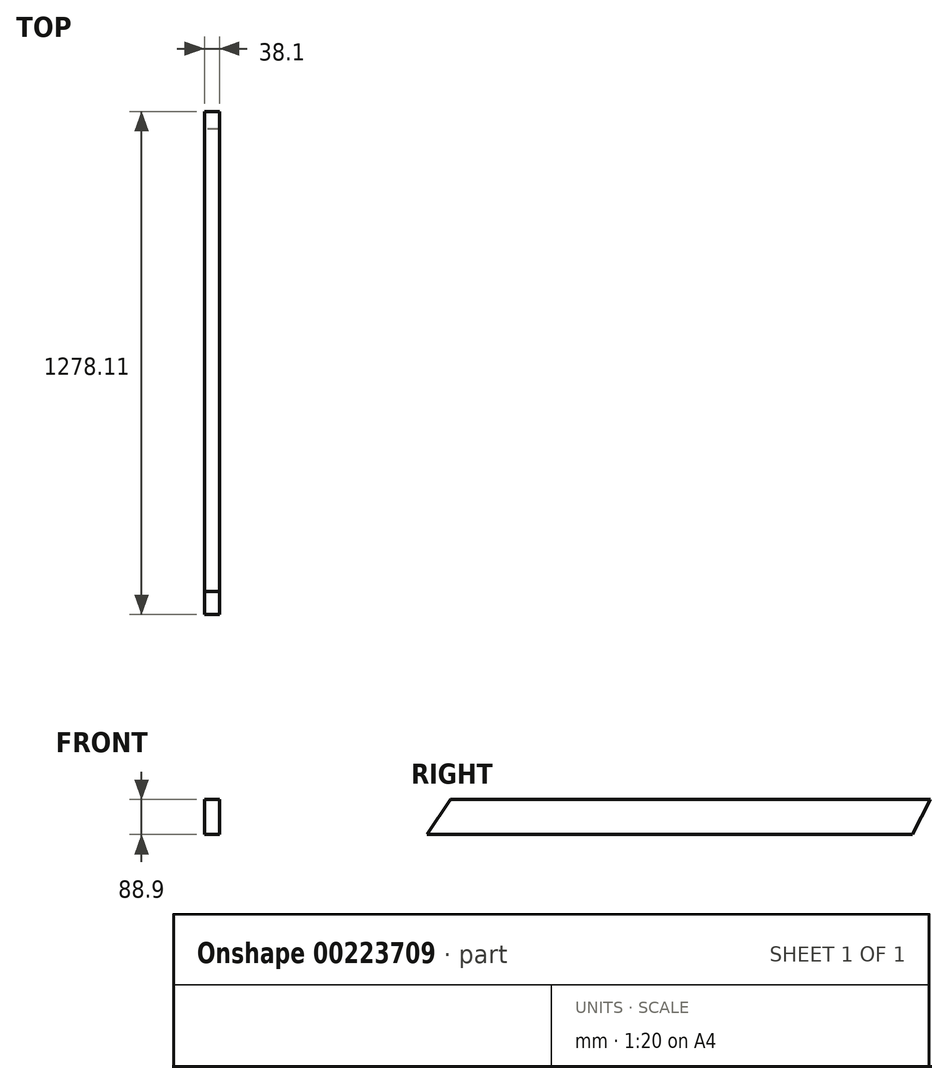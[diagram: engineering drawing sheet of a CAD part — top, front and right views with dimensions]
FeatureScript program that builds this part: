
annotation { "Feature Type Name" : "Feature", "Feature Type Description" : "" }
export const myFeature = defineFeature(function(context is Context, id is Id, definition is map)
    precondition{}
    {
        {
            var Q0;
            Q0=qCreatedBy(makeId("Right.planeOp"),FACE);
            var sketch = newSketch(context, id + "F0", { "sketchPlane" : qUnion([Q0])});
            skLineSegment(sketch, "E0.bottom", {"start": v(-609.42, -26.03) * mm, "end": v(609.78, -26.03) * mm});
            skLineSegment(sketch, "E0.top", {"start": v(-668.33, -114.93) * mm, "end": v(564.48, -114.93) * mm});
            skLineSegment(sketch, "E1", {"start": v(609.78, -26.03) * mm, "end": v(564.48, -114.93) * mm});
            skLineSegment(sketch, "E2", {"start": v(-609.42, -26.03) * mm, "end": v(-668.37, -114.98) * mm});
            skSolve(sketch);
        }
        {
            var Q0;
            Q0 = qSketchRegion(id + "F0", true);
            extrude(context, id + "F1", {"entities" : qUnion([Q0]), "depth" : 38.1 * mm});
        }
    });
